# Revit family: Reece_Basin_American Standard_Studio_Wall Basin_350 mm
name_source: partatom
category: Plumbing Fixtures
revit_build: Autodesk Revit 2018 (Build: 20190510_1515(x64)
units: mm (PartAtom-declared; Revit-internal decimal feet)

## family parameters
Always vertical = Yes
Cut with Voids When Loaded = Yes
Part Type = Normal
Room Calculation Point = Yes
Round Connector Dimension = Use Diameter
Shared = Yes
Work Plane-Based = Yes

## types (1)
- 1 Taphole_Vitreous China
    Default Elevation = 0 mm  [stored 0 ft]
    Description = American Standard Studio Wall Basin with Fixing Kit 1 Taphole 350mm White
    Disclaimer = THIS FILE IS THE PROPERTY OF THE REECE GROUP. IT MAY NOT BE REPRODUCED, REVERSE-ENGINEERED OR MODIFIED. ANY REPUBLICATION, TRANSMISSION OR DISTRIBUTION FOR THE PURPOSE OF COMMERCIALLY EXPLOITING THE FILES IS PROHIBITED.
    Keynote = Product #9506444, Reece_Basin_American Standard_Studio_Wall Basin_350 mm - 1 Taphole_Vitreous China
    Manufacturer = American Standard
    Model = Studio
    Reece_Basin_Outlet = 40 mm  [stored 0.131234 ft]
    Reece_Detail_Additional = With Fixing
    Reece_Detail_Connector = 1 Taphole
    Reece_Detail_Disclaimer = THIS FILE IS THE PROPERTY OF THE REECE GROUP. IT MAY NOT BE REPRODUCED, REVERSE-ENGINEERED OR MODIFIED. ANY REPUBLICATION, TRANSMISSION OR DISTRIBUTION FOR THE PURPOSE OF COMMERCIALLY EXPLOITING THE FILES IS PROHIBITED.
    Reece_Detail_Installation = Wall Basin
    Reece_Material_Main = Reece_Vitreous China_White
    Reece_Material_Secondary = Reece_Brass_Chrome
    Reece_Overall_Capacity = 1.2 L
    Reece_Overall_Depth = 250 mm  [stored 0.82021 ft]
    Reece_Overall_Height = 140 mm  [stored 0.459318 ft]
    Reece_Overall_Width = 350 mm
    Reece_Product_Brand = American Standard
    Reece_Product_Description = American Standard Studio Wall Basin with Fixing Kit 1 Taphole 350mm White
    Reece_Product_Mount = Wall Mounted
    Reece_Product_Number = 9506444
    Reece_Product_Sub Brand = Studio
    Reece_Product_Type = Basin
    Reece_Product_Web Page = https://www.reece.com.au
    Type Comments = Basin
    URL = https://www.reece.com.au

note: [stored X ft] marks values corroborated as IEEE doubles in the binary element streams (Revit-internal decimal feet)

## geometry (parser evidence)
native form markers: Sweep x6
no freeform markers — native parametric forms only
